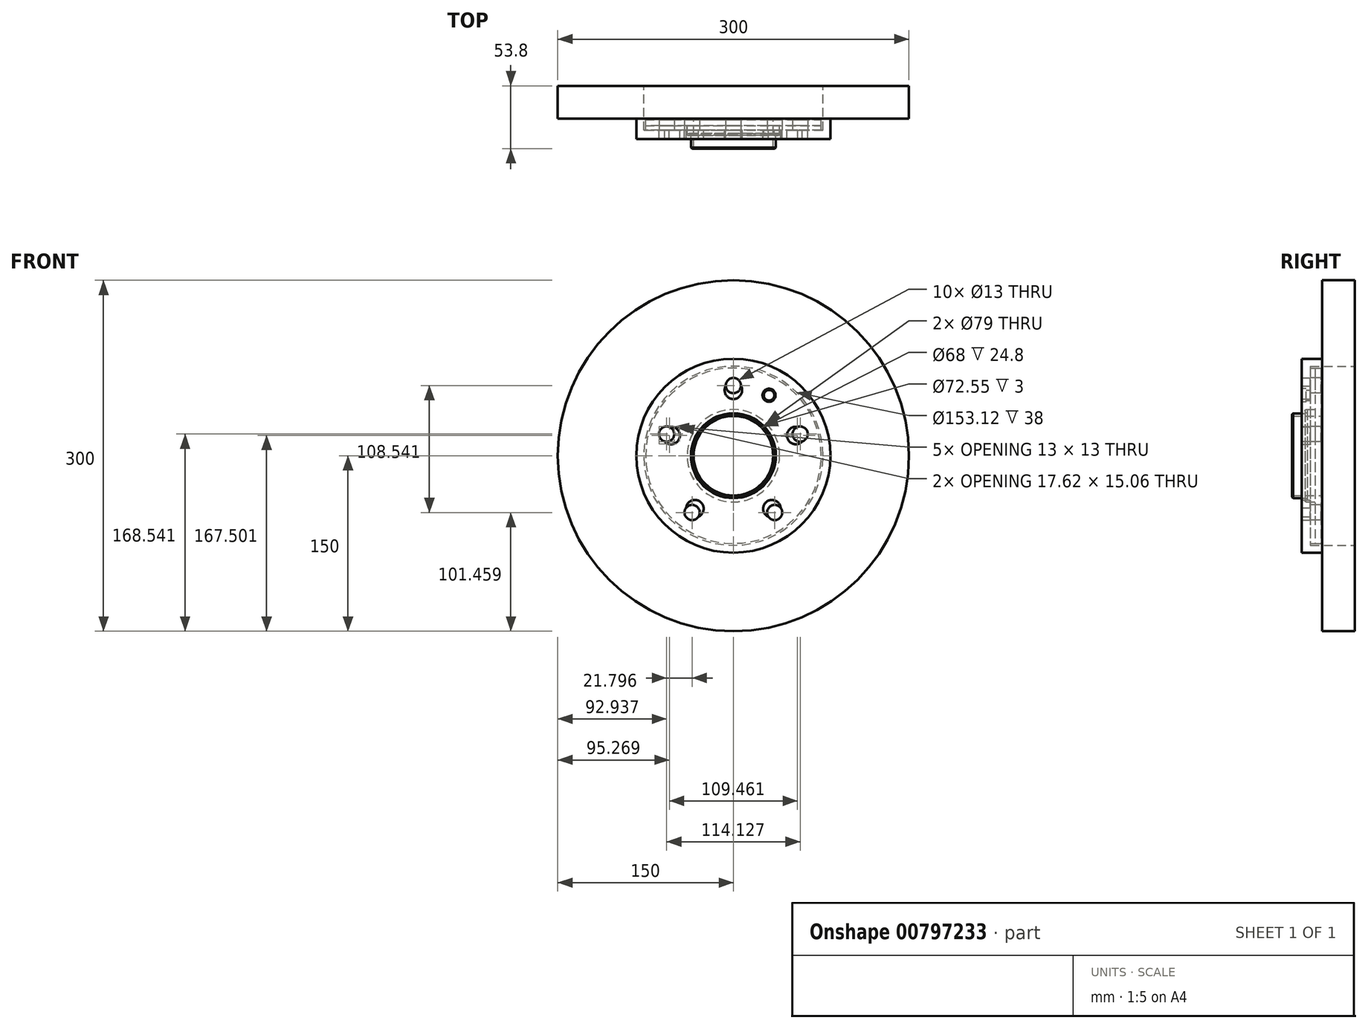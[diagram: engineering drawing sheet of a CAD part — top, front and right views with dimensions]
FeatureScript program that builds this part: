
annotation { "Feature Type Name" : "Feature", "Feature Type Description" : "" }
export const myFeature = defineFeature(function(context is Context, id is Id, definition is map)
    precondition{}
    {
        {
            var Q0;
            Q0=qCreatedBy(makeId("Front.planeOp"),FACE);
            var sketch = newSketch(context, id + "F0", { "sketchPlane" : qUnion([Q0])});
            skCircle(sketch, "E0", {"center": v(0, 0) * mm, "radius": 56 * mm, "construction": true});
            skCircle(sketch, "E1", {"center": v(0, 0) * mm, "radius": 60 * mm, "construction": true});
            skLineSegment(sketch, "E2", {"start": v(0, 0) * mm, "end": v(0, 83.36) * mm, "construction": true});
            skCircle(sketch, "E3", {"center": v(0, 56) * mm, "radius": 7.5 * mm});
            skCircle(sketch, "E4.1.0", {"center": v(-53.26, 17.3) * mm, "radius": 7.5 * mm});
            skCircle(sketch, "E4.2.0", {"center": v(-32.92, -45.3) * mm, "radius": 7.5 * mm});
            skCircle(sketch, "E4.3.0", {"center": v(32.92, -45.3) * mm, "radius": 7.5 * mm});
            skCircle(sketch, "E4.4.0", {"center": v(53.26, 17.3) * mm, "radius": 7.5 * mm});
            skCircle(sketch, "E5", {"center": v(0, 60) * mm, "radius": 6.5 * mm});
            skCircle(sketch, "E6.1.0", {"center": v(-57.06, 18.54) * mm, "radius": 6.5 * mm});
            skCircle(sketch, "E6.2.0", {"center": v(-35.27, -48.54) * mm, "radius": 6.5 * mm});
            skCircle(sketch, "E6.3.0", {"center": v(35.27, -48.54) * mm, "radius": 6.5 * mm});
            skCircle(sketch, "E6.4.0", {"center": v(57.06, 18.54) * mm, "radius": 6.5 * mm});
            skLineSegment(sketch, "E7", {"start": v(0, 0) * mm, "end": v(39.3, 66.72) * mm, "construction": true});
            skCircle(sketch, "E8", {"center": v(30.45, 51.7) * mm, "radius": 4.5 * mm});
            skSolve(sketch);
        }
        {
            var Q0;
            Q0=qCreatedBy(makeId("Right.planeOp"),FACE);
            var sketch = newSketch(context, id + "F1", { "sketchPlane" : qUnion([Q0])});
            skLineSegment(sketch, "E9", {"start": v(0, 0) * mm, "end": v(138.28, 0) * mm, "construction": true});
            skLineSegment(sketch, "E10", {"start": v(0, 0) * mm, "end": v(-72.89, 0) * mm, "construction": true});
            skLineSegment(sketch, "E11", {"start": v(9, 34) * mm, "end": v(-15.8, 34) * mm});
            skLineSegment(sketch, "E12", {"start": v(-15.8, 34) * mm, "end": v(-15.8, 36.25) * mm});
            skLineSegment(sketch, "E13", {"start": v(-15.8, 36.25) * mm, "end": v(-4.2, 36.25) * mm});
            skLineSegment(sketch, "E14", {"start": v(-2.7, 37.75) * mm, "end": v(-2.7, 39.48) * mm});
            skLineSegment(sketch, "E15", {"start": v(-2.7, 39.48) * mm, "end": v(4, 39.48) * mm});
            skLineSegment(sketch, "E16", {"start": v(4, 39.48) * mm, "end": v(4, 75) * mm});
            skLineSegment(sketch, "E17", {"start": v(4, 75) * mm, "end": v(9, 75) * mm});
            skLineSegment(sketch, "E18", {"start": v(9, 75) * mm, "end": v(9, 34) * mm});
            skLineSegment(sketch, "E19.0", {"start": v(0, -60) * mm, "end": v(0, 60) * mm, "construction": true});
            skLineSegment(sketch, "E20", {"start": v(4, 39.5) * mm, "end": v(0, 39.5) * mm});
            skLineSegment(sketch, "E21", {"start": v(0, 39.5) * mm, "end": v(0, 75) * mm});
            skLineSegment(sketch, "E22", {"start": v(0, 75) * mm, "end": v(4, 75) * mm});
            skLineSegment(sketch, "E23", {"start": v(-7.5, 36.28) * mm, "end": v(-7.5, 82.9) * mm});
            skLineSegment(sketch, "E24", {"start": v(-7.5, 82.9) * mm, "end": v(38, 82.9) * mm});
            skLineSegment(sketch, "E25", {"start": v(38, 82.9) * mm, "end": v(38, 76.56) * mm});
            skLineSegment(sketch, "E26", {"start": v(38, 76.56) * mm, "end": v(0, 76.56) * mm});
            skLineSegment(sketch, "E27", {"start": v(0, 76.56) * mm, "end": v(0, 42.78) * mm});
            skLineSegment(sketch, "E28", {"start": v(-4.5, 36.28) * mm, "end": v(-7.5, 36.28) * mm});
            skPoint(sketch, "E29.visualSharp", {"position": v(-2.7, 36.25) * mm});
            skArc(sketch, "E29.filletArc", {"start": v(-4.2, 36.25) * mm, "mid": v(-3.14, 36.69) * mm, "end": v(-2.7, 37.75) * mm});
            skLineSegment(sketch, "E30", {"start": v(-4.5, 36.28) * mm, "end": v(-4.5, 38.5) * mm});
            skLineSegment(sketch, "E31", {"start": v(-3.5, 39.5) * mm, "end": v(0, 39.5) * mm});
            skLineSegment(sketch, "E32", {"start": v(0, 39.5) * mm, "end": v(0, 42.78) * mm});
            skPoint(sketch, "E33.visualSharp", {"position": v(-4.5, 39.5) * mm});
            skArc(sketch, "E33.filletArc", {"start": v(-3.5, 39.5) * mm, "mid": v(-4.2, 39.2) * mm, "end": v(-4.5, 38.5) * mm});
            skLineSegment(sketch, "E34", {"start": v(-15.8, 35.25) * mm, "end": v(-14.8, 36.25) * mm});
            skLineSegment(sketch, "E35", {"start": v(38, 82.9) * mm, "end": v(38, 150) * mm});
            skLineSegment(sketch, "E36", {"start": v(10, 150) * mm, "end": v(10, 82.9) * mm});
            skLineSegment(sketch, "E37", {"start": v(38, 150) * mm, "end": v(10, 150) * mm});
            skSolve(sketch);
        }
        {
            var Q0;
            {var subQ5=sQuery(id+"F1.wireOp",EDGE,"E11");Q0=makeQuery(id+"F1.imprint","IMPRINT",FACE,{"disambiguationData":[TD([[makeQuery(id+"F1.imprint","IMPRINT",EDGE,{"derivedFrom":subQ5}),-1.0]])]});}
            var Q1;
            Q1=sQuery(id+"F1.wireOp",EDGE,"E10");
            revolve(context, id + "F2", {"surfaceOperationType" : NewSurfaceOperationType.NEW, "entities" : qUnion([Q0]), "axis" : qUnion([Q1]), "revolveType" : RevolveType.FULL});
        }
        {
            var Q0;
            {var subQ2=sQuery(id+"F1.wireOp",EDGE,"E20");Q0=makeQuery(id+"F1.imprint","IMPRINT",FACE,{"disambiguationData":[TD([[makeQuery(id+"F1.imprint","IMPRINT",EDGE,{"derivedFrom":subQ2}),-1.0]])]});}
            var Q1;
            Q1=sQuery(id+"F1.wireOp",EDGE,"E10");
            revolve(context, id + "F3", {"surfaceOperationType" : NewSurfaceOperationType.NEW, "entities" : qUnion([Q0]), "axis" : qUnion([Q1]), "revolveType" : RevolveType.FULL});
        }
        {
            var Q0;
            Q0=makeQuery(id+"F1.imprint","IMPRINT",FACE,{"disambiguationData":[TD([[makeQuery(id+"F1.imprint","IMPRINT",EDGE,{"derivedFrom":sQuery(id+"F1.wireOp",EDGE,"E23")}),-1.0]])]});
            var Q1;
            {var subQ1=sQuery(id+"F1.wireOp",EDGE,"E35");Q1=makeQuery(id+"F1.imprint","IMPRINT",FACE,{"disambiguationData":[TD([[makeQuery(id+"F1.imprint","IMPRINT",EDGE,{"derivedFrom":subQ1}),1.0]])]});}
            var Q2;
            Q2=sQuery(id+"F1.wireOp",EDGE,"E10");
            revolve(context, id + "F4", {"surfaceOperationType" : NewSurfaceOperationType.NEW, "entities" : qUnion([Q0, Q1]), "axis" : qUnion([Q2]), "revolveType" : RevolveType.FULL});
        }
        {
            var Q0;
            {var subQ0=sQuery(id+"F0.wireOp",EDGE,"E6.4.0");var subQ1=sQuery(id+"F0.wireOp",EDGE,"E4.4.0");var subQ2=makeQuery(id+"F0.imprint","INTERSECT",VERTEX,{"disambiguationData":[OD(0.0)],"derivedFrom":[subQ1,subQ0]});Q0=makeQuery(id+"F0.imprint","IMPRINT",FACE,{"disambiguationData":[TD([[makeQuery(id+"F0.imprint","IMPRINT",EDGE,{"disambiguationData":[TD([[subQ2,1.0]])],"derivedFrom":subQ1}),-1.0]])]});}
            var Q1;
            {var subQ0=sQuery(id+"F0.wireOp",EDGE,"E6.4.0");var subQ1=sQuery(id+"F0.wireOp",EDGE,"E4.4.0");var subQ2=makeQuery(id+"F0.imprint","INTERSECT",VERTEX,{"disambiguationData":[OD(0.0)],"derivedFrom":[subQ1,subQ0]});Q1=makeQuery(id+"F0.imprint","IMPRINT",FACE,{"disambiguationData":[TD([[makeQuery(id+"F0.imprint","IMPRINT",EDGE,{"disambiguationData":[TD([[subQ2,1.0]])],"derivedFrom":subQ1}),1.0]])]});}
            var Q2;
            {var subQ0=sQuery(id+"F0.wireOp",EDGE,"E5");var subQ1=sQuery(id+"F0.wireOp",EDGE,"E3");var subQ2=makeQuery(id+"F0.imprint","INTERSECT",VERTEX,{"disambiguationData":[OD(0.0)],"derivedFrom":[subQ1,subQ0]});Q2=makeQuery(id+"F0.imprint","IMPRINT",FACE,{"disambiguationData":[TD([[makeQuery(id+"F0.imprint","IMPRINT",EDGE,{"disambiguationData":[TD([[subQ2,1.0]])],"derivedFrom":subQ1}),-1.0]])]});}
            var Q3;
            {var subQ0=sQuery(id+"F0.wireOp",EDGE,"E5");var subQ1=sQuery(id+"F0.wireOp",EDGE,"E3");var subQ2=makeQuery(id+"F0.imprint","INTERSECT",VERTEX,{"disambiguationData":[OD(0.0)],"derivedFrom":[subQ1,subQ0]});Q3=makeQuery(id+"F0.imprint","IMPRINT",FACE,{"disambiguationData":[TD([[makeQuery(id+"F0.imprint","IMPRINT",EDGE,{"disambiguationData":[TD([[subQ2,1.0]])],"derivedFrom":subQ1}),1.0]])]});}
            var Q4;
            {var subQ0=sQuery(id+"F0.wireOp",EDGE,"E6.1.0");var subQ1=sQuery(id+"F0.wireOp",EDGE,"E4.1.0");var subQ2=makeQuery(id+"F0.imprint","INTERSECT",VERTEX,{"disambiguationData":[OD(0.0)],"derivedFrom":[subQ1,subQ0]});Q4=makeQuery(id+"F0.imprint","IMPRINT",FACE,{"disambiguationData":[TD([[makeQuery(id+"F0.imprint","IMPRINT",EDGE,{"disambiguationData":[TD([[subQ2,1.0]])],"derivedFrom":subQ1}),-1.0]])]});}
            var Q5;
            {var subQ0=sQuery(id+"F0.wireOp",EDGE,"E6.1.0");var subQ1=sQuery(id+"F0.wireOp",EDGE,"E4.1.0");var subQ2=makeQuery(id+"F0.imprint","INTERSECT",VERTEX,{"disambiguationData":[OD(0.0)],"derivedFrom":[subQ1,subQ0]});Q5=makeQuery(id+"F0.imprint","IMPRINT",FACE,{"disambiguationData":[TD([[makeQuery(id+"F0.imprint","IMPRINT",EDGE,{"disambiguationData":[TD([[subQ2,1.0]])],"derivedFrom":subQ1}),1.0]])]});}
            var Q6;
            {var subQ0=sQuery(id+"F0.wireOp",EDGE,"E6.2.0");var subQ1=sQuery(id+"F0.wireOp",EDGE,"E4.2.0");var subQ2=makeQuery(id+"F0.imprint","INTERSECT",VERTEX,{"disambiguationData":[OD(0.0)],"derivedFrom":[subQ1,subQ0]});Q6=makeQuery(id+"F0.imprint","IMPRINT",FACE,{"disambiguationData":[TD([[makeQuery(id+"F0.imprint","IMPRINT",EDGE,{"disambiguationData":[TD([[subQ2,-1.0]])],"derivedFrom":subQ1}),-1.0]])]});}
            var Q7;
            {var subQ0=sQuery(id+"F0.wireOp",EDGE,"E6.2.0");var subQ1=sQuery(id+"F0.wireOp",EDGE,"E4.2.0");var subQ2=makeQuery(id+"F0.imprint","INTERSECT",VERTEX,{"disambiguationData":[OD(0.0)],"derivedFrom":[subQ1,subQ0]});Q7=makeQuery(id+"F0.imprint","IMPRINT",FACE,{"disambiguationData":[TD([[makeQuery(id+"F0.imprint","IMPRINT",EDGE,{"disambiguationData":[TD([[subQ2,-1.0]])],"derivedFrom":subQ1}),1.0]])]});}
            var Q8;
            {var subQ0=sQuery(id+"F0.wireOp",EDGE,"E6.3.0");var subQ1=sQuery(id+"F0.wireOp",EDGE,"E4.3.0");var subQ2=makeQuery(id+"F0.imprint","INTERSECT",VERTEX,{"disambiguationData":[OD(0.0)],"derivedFrom":[subQ1,subQ0]});Q8=makeQuery(id+"F0.imprint","IMPRINT",FACE,{"disambiguationData":[TD([[makeQuery(id+"F0.imprint","IMPRINT",EDGE,{"disambiguationData":[TD([[subQ2,-1.0]])],"derivedFrom":subQ1}),-1.0]])]});}
            var Q9;
            {var subQ0=sQuery(id+"F0.wireOp",EDGE,"E6.3.0");var subQ1=sQuery(id+"F0.wireOp",EDGE,"E4.3.0");var subQ2=makeQuery(id+"F0.imprint","INTERSECT",VERTEX,{"disambiguationData":[OD(0.0)],"derivedFrom":[subQ1,subQ0]});Q9=makeQuery(id+"F0.imprint","IMPRINT",FACE,{"disambiguationData":[TD([[makeQuery(id+"F0.imprint","IMPRINT",EDGE,{"disambiguationData":[TD([[subQ2,-1.0]])],"derivedFrom":subQ1}),1.0]])]});}
            extrude(context, id + "F5", {"entities" : qUnion([Q0, Q1, Q2, Q3, Q4, Q5, Q6, Q7, Q8, Q9]), "operationType" : NewBodyOperationType.REMOVE, "oppositeDirection" : true, "depth" : 25 * mm, "offsetDistance" : 25 * mm});
        }
        {
            var Q0;
            Q0 = qSketchRegion(id + "F0", true);
            extrude(context, id + "F6", {"entities" : qUnion([Q0]), "operationType" : NewBodyOperationType.REMOVE, "depth" : 25 * mm, "offsetDistance" : 25 * mm});
        }
        {
            var Q0;
            Q0=makeQuery(id+"F4.opRevolve","SWEPT_FACE",FACE,{"disambiguationData":[OSD([sQuery(id+"F1.wireOp",EDGE,"E23")])]});
            var sketch = newSketch(context, id + "F7", { "sketchPlane" : qUnion([Q0])});
            skCircle(sketch, "E38.0", {"center": v(30.45, 51.7) * mm, "radius": 4.5 * mm, "construction": true});
            skCircle(sketch, "E39", {"center": v(30.45, 51.7) * mm, "radius": 5.6 * mm});
            skSolve(sketch);
        }
        {
            var Q0;
            Q0 = qSketchRegion(id + "F7", true);
            extrude(context, id + "F8", {"entities" : qUnion([Q0]), "operationType" : NewBodyOperationType.REMOVE, "oppositeDirection" : true, "depth" : 4 * mm, "offsetDistance" : 25 * mm});
        }
    });
